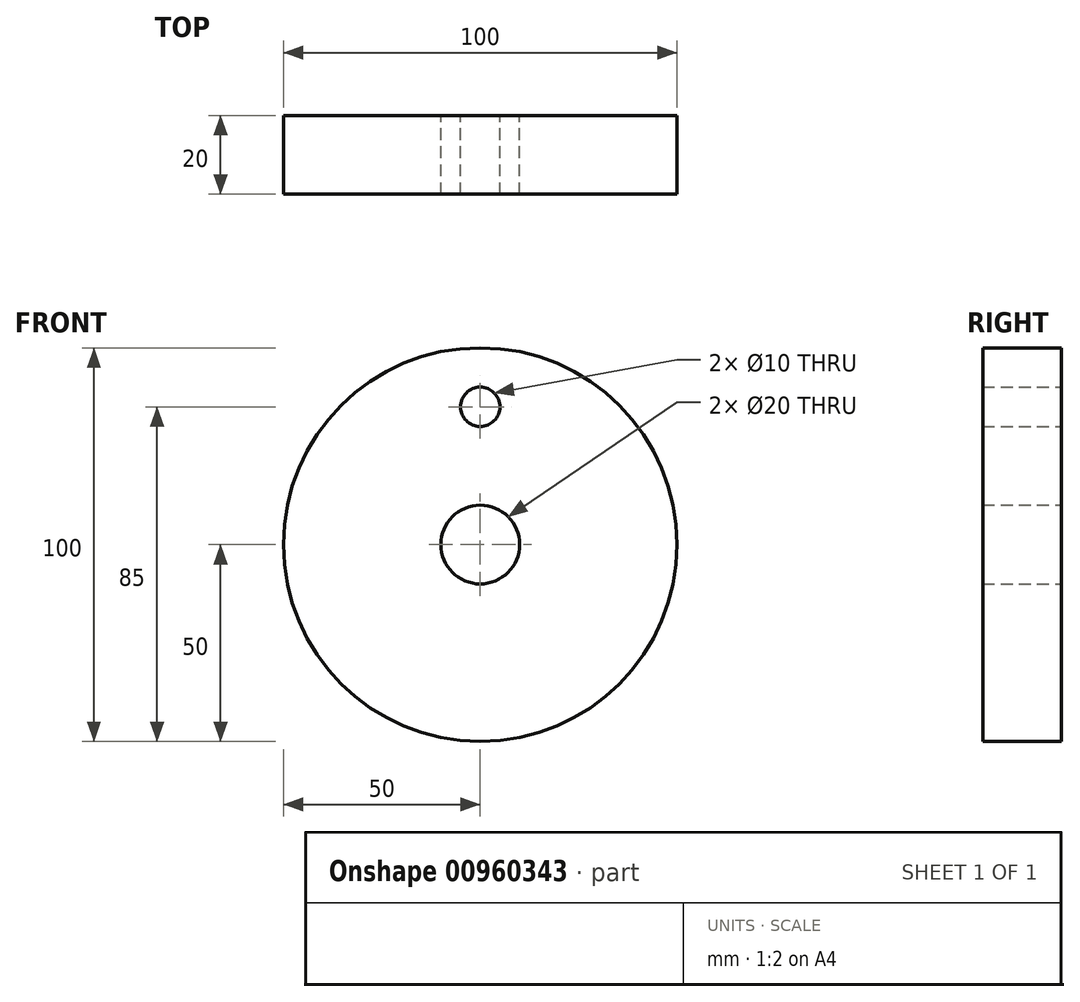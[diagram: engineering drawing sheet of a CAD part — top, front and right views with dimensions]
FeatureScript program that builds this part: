
annotation { "Feature Type Name" : "Feature", "Feature Type Description" : "" }
export const myFeature = defineFeature(function(context is Context, id is Id, definition is map)
    precondition{}
    {
        {
            var Q0;
            Q0=qCreatedBy(makeId("Front.planeOp"),FACE);
            var sketch = newSketch(context, id + "F0", { "sketchPlane" : qUnion([Q0])});
            skCircle(sketch, "E0", {"center": v(0, 0) * mm, "radius": 50 * mm});
            skCircle(sketch, "E1", {"center": v(0, 35) * mm, "radius": 5 * mm});
            skLineSegment(sketch, "E2", {"start": v(-71.27, 0) * mm, "end": v(71.27, 0) * mm, "construction": true});
            skLineSegment(sketch, "E3", {"start": v(0, 71.45) * mm, "end": v(0, -71.45) * mm, "construction": true});
            skCircle(sketch, "E4", {"center": v(0, 0) * mm, "radius": 10 * mm});
            skSolve(sketch);
        }
        {
            var Q0;
            Q0 = qSketchRegion(id + "F0", true);
            extrude(context, id + "F1", {"entities" : qUnion([Q0]), "depth" : 20 * mm, "offsetDistance" : 25 * mm});
        }
    });
